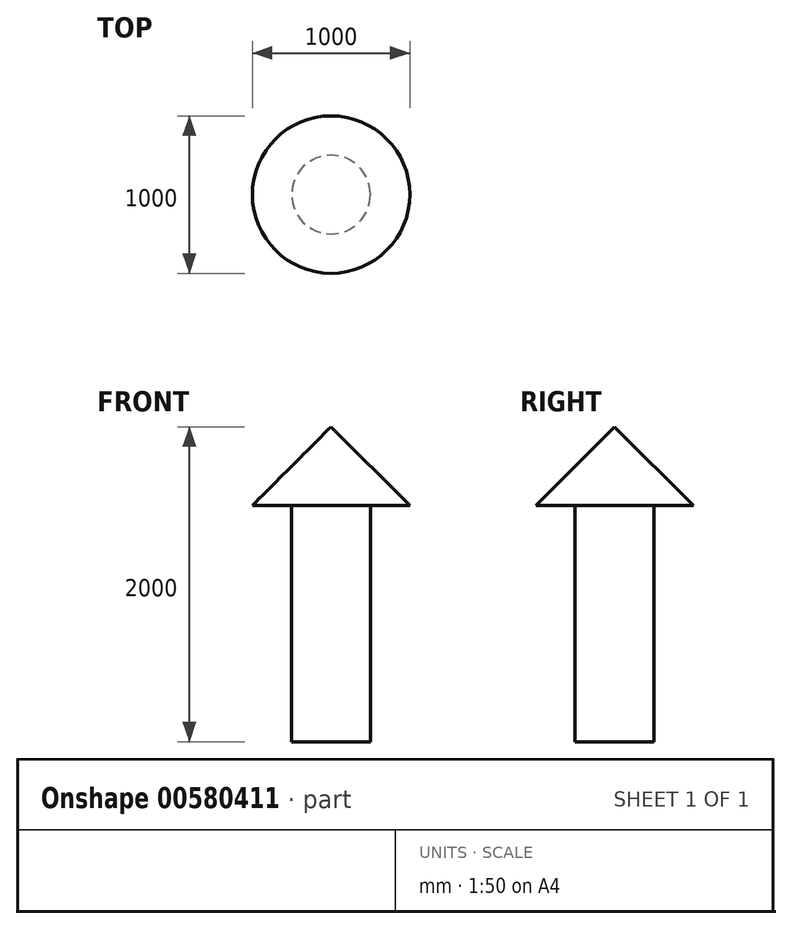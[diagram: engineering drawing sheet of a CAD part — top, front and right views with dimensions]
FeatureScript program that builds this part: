
annotation { "Feature Type Name" : "Feature", "Feature Type Description" : "" }
export const myFeature = defineFeature(function(context is Context, id is Id, definition is map)
    precondition{}
    {
        {
            var Q0;
            Q0=qCreatedBy(makeId("Top.planeOp"),FACE);
            var sketch = newSketch(context, id + "F0", { "sketchPlane" : qUnion([Q0])});
            skCircle(sketch, "E0", {"center": v(0, 0) * mm, "radius": 250 * mm});
            skSolve(sketch);
        }
        {
            var Q0;
            Q0 = qSketchRegion(id + "F0", true);
            extrude(context, id + "F1", {"entities" : qUnion([Q0]), "oppositeDirection" : true, "depth" : 1500 * mm, "offsetDistance" : 25 * mm});
        }
        {
            var Q0;
            Q0=qCreatedBy(makeId("Front.planeOp"),FACE);
            var sketch = newSketch(context, id + "F2", { "sketchPlane" : qUnion([Q0])});
            skLineSegment(sketch, "E1", {"start": v(0, 0) * mm, "end": v(0, 500) * mm});
            skLineSegment(sketch, "E2", {"start": v(0, 0) * mm, "end": v(500, 0) * mm});
            skLineSegment(sketch, "E3", {"start": v(500, 0) * mm, "end": v(0, 500) * mm});
            skSolve(sketch);
        }
        {
            var Q0;
            Q0=makeQuery(id+"F2.imprint","IMPRINT",FACE,{"disambiguationData":[TD([[makeQuery(id+"F2.imprint","IMPRINT",EDGE,{"derivedFrom":sQuery(id+"F2.wireOp",EDGE,"E1")}),-1.0]])]});
            var Q1;
            Q1=sQuery(id+"F2.wireOp",EDGE,"E1");
            revolve(context, id + "F3", {"operationType" : NewBodyOperationType.ADD, "entities" : qUnion([Q0]), "axis" : qUnion([Q1]), "revolveType" : RevolveType.FULL});
        }
    });
